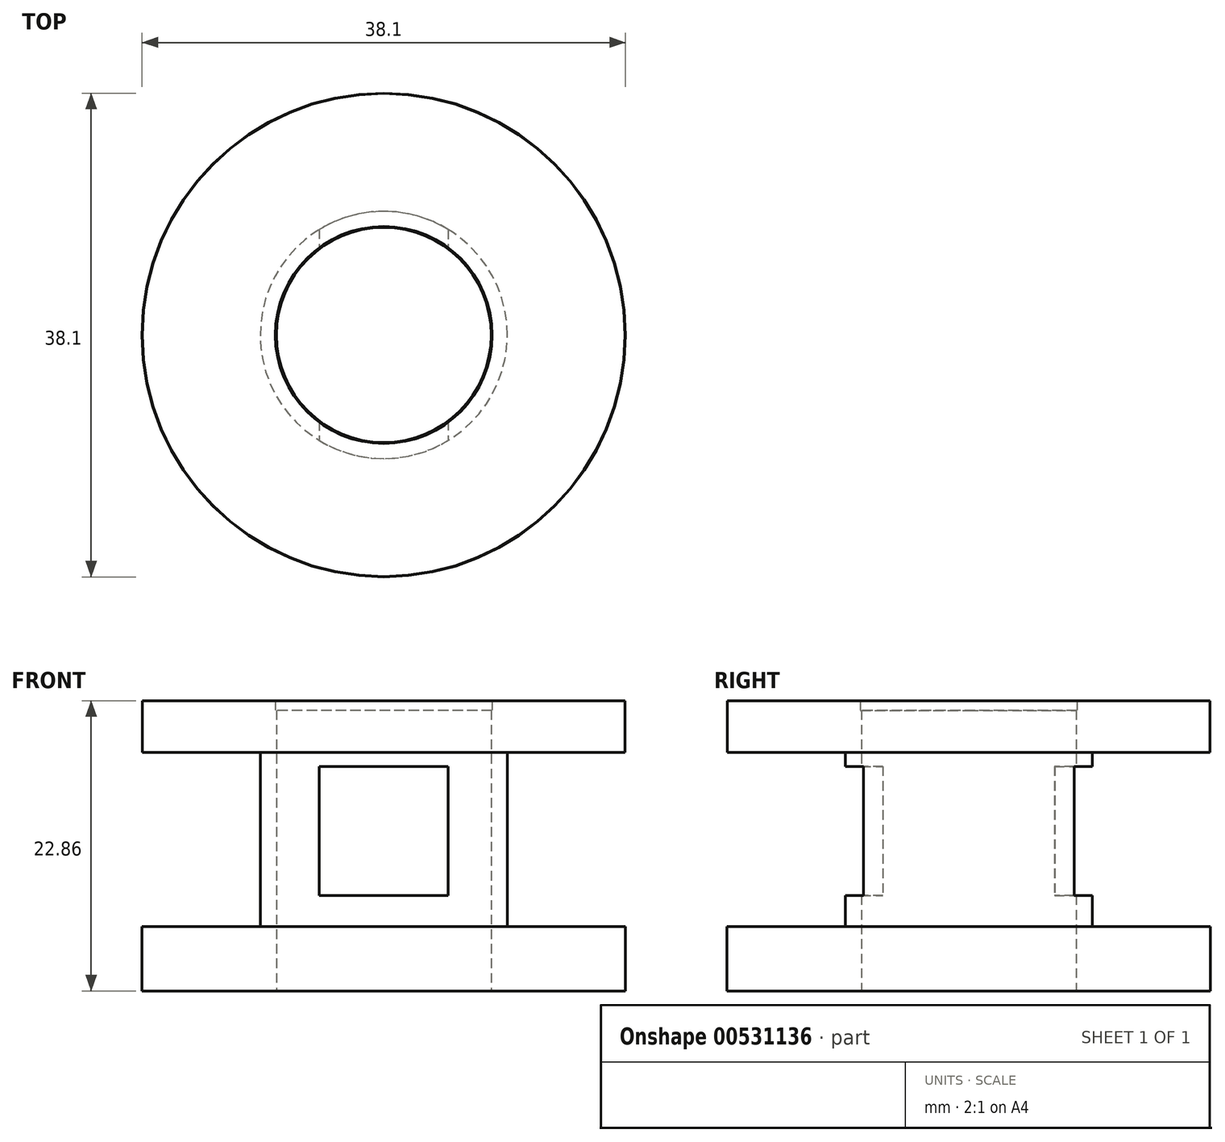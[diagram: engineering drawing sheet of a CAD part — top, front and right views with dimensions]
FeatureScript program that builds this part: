
annotation { "Feature Type Name" : "Feature", "Feature Type Description" : "" }
export const myFeature = defineFeature(function(context is Context, id is Id, definition is map)
    precondition{}
    {
        {
            var Q0;
            Q0=qCreatedBy(makeId("Top.planeOp"),FACE);
            var sketch = newSketch(context, id + "F0", { "sketchPlane" : qUnion([Q0])});
            skCircle(sketch, "E0", {"center": v(0, 0) * mm, "radius": 19.05 * mm});
            skCircle(sketch, "E1", {"center": v(0, 0) * mm, "radius": 9.74 * mm});
            skCircle(sketch, "E2.0", {"center": v(0, 0) * mm, "radius": 8.47 * mm});
            skSolve(sketch);
        }
        {
            var Q0;
            Q0 = qSketchRegion(id + "F0", true);
            extrude(context, id + "F1", {"entities" : qUnion([Q0]), "depth" : 5.08 * mm, "offsetDistance" : 25.4 * mm});
        }
        {
            var Q0;
            Q0=makeQuery(id+"F0.imprint","IMPRINT",FACE,{"disambiguationData":[TD([[makeQuery(id+"F0.imprint","IMPRINT",EDGE,{"derivedFrom":sQuery(id+"F0.wireOp",EDGE,"E1")}),1.0]])]});
            extrude(context, id + "F2", {"entities" : qUnion([Q0]), "operationType" : NewBodyOperationType.ADD, "depth" : 22.1 * mm, "offsetDistance" : 25.4 * mm});
        }
        {
            var Q0;
            Q0=qCreatedBy(makeId("Top.planeOp"),FACE);
            var sketch = newSketch(context, id + "F3", { "sketchPlane" : qUnion([Q0])});
            skCircle(sketch, "E3", {"center": v(0, 0) * mm, "radius": 8.55 * mm});
            skCircle(sketch, "E4", {"center": v(0, 0) * mm, "radius": 19.02 * mm});
            skSolve(sketch);
        }
        {
            var Q0;
            Q0 = qSketchRegion(id + "F3", true);
            extrude(context, id + "F4", {"entities" : qUnion([Q0]), "operationType" : NewBodyOperationType.ADD, "depth" : 22.86 * mm, "offsetDistance" : 25.4 * mm, "hasSecondDirection" : true, "secondDirectionOppositeDirection" : false, "secondDirectionDepth" : 18.8 * mm});
        }
        {
            var Q0;
            Q0=qCreatedBy(makeId("Front.planeOp"),FACE);
            var sketch = newSketch(context, id + "F5", { "sketchPlane" : qUnion([Q0])});
            skLineSegment(sketch, "E5.bottom", {"start": v(-5.07, 17.68) * mm, "end": v(5.09, 17.68) * mm});
            skLineSegment(sketch, "E5.top", {"start": v(-5.07, 7.52) * mm, "end": v(5.09, 7.52) * mm});
            skLineSegment(sketch, "E5.left", {"start": v(-5.07, 17.68) * mm, "end": v(-5.07, 7.52) * mm});
            skLineSegment(sketch, "E5.right", {"start": v(5.09, 17.68) * mm, "end": v(5.09, 7.52) * mm});
            skSolve(sketch);
        }
        {
            var Q0;
            Q0 = qSketchRegion(id + "F5", true);
            extrude(context, id + "F6", {"entities" : qUnion([Q0]), "operationType" : NewBodyOperationType.REMOVE, "oppositeDirection" : true, "depth" : 13.72 * mm, "offsetDistance" : 25.4 * mm, "hasSecondDirection" : true, "secondDirectionOppositeDirection" : false, "secondDirectionDepth" : 12.45 * mm});
        }
    });
